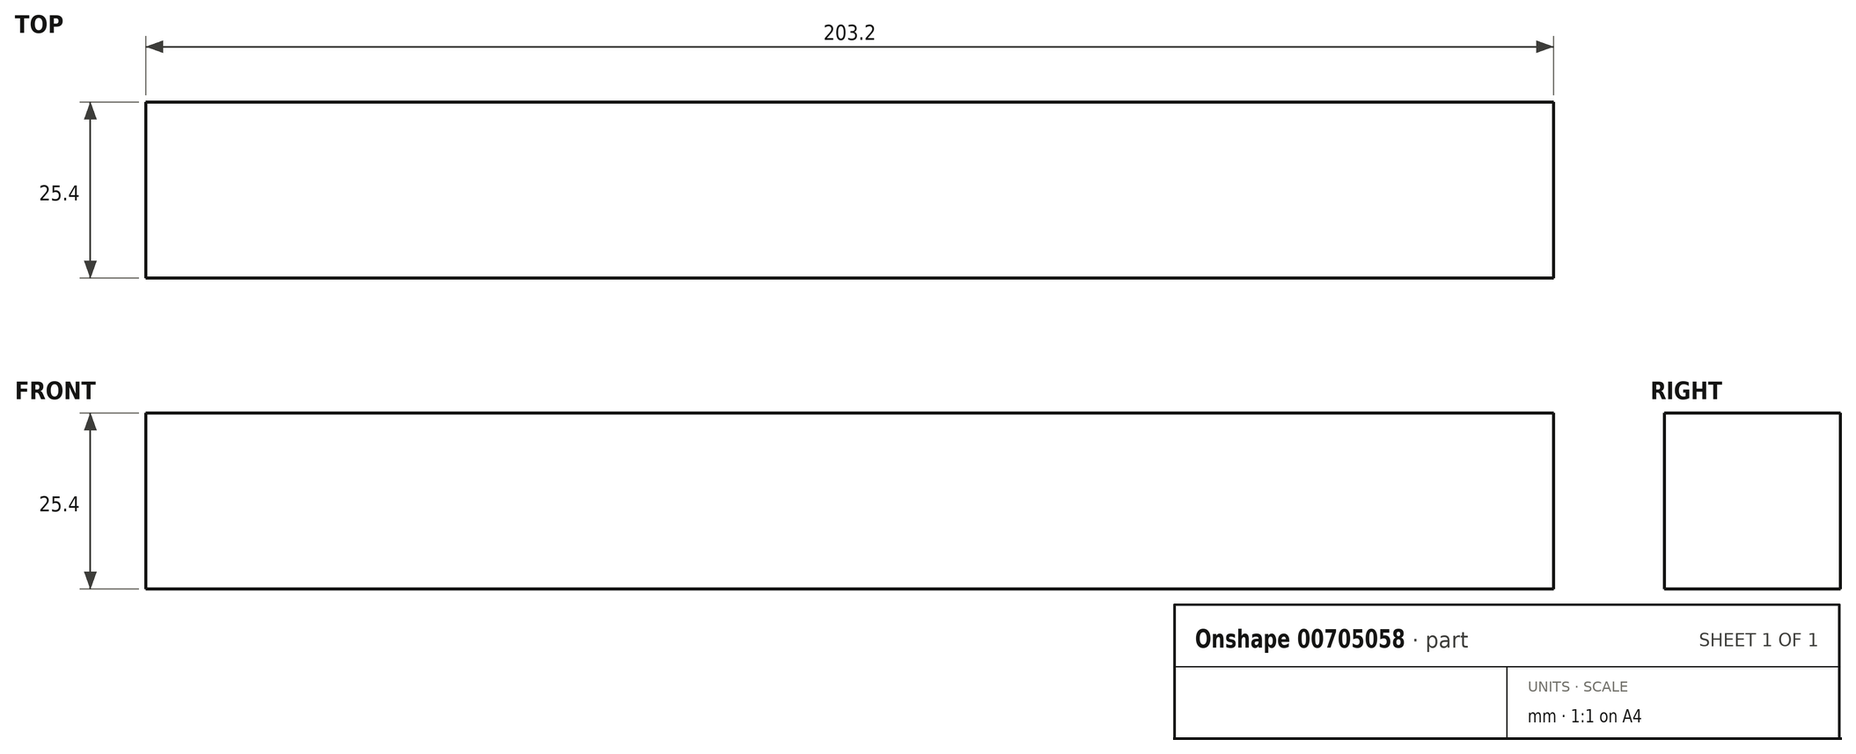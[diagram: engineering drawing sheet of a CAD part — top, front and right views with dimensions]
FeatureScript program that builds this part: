
annotation { "Feature Type Name" : "Feature", "Feature Type Description" : "" }
export const myFeature = defineFeature(function(context is Context, id is Id, definition is map)
    precondition{}
    {
        {
            var Q0;
            Q0=qCreatedBy(makeId("Top.planeOp"),FACE);
            var sketch = newSketch(context, id + "F0", { "sketchPlane" : qUnion([Q0])});
            skLineSegment(sketch, "E0.bottom", {"start": v(0, 0) * mm, "end": v(-203.2, 0) * mm});
            skLineSegment(sketch, "E0.top", {"start": v(0, 25.4) * mm, "end": v(-203.2, 25.4) * mm});
            skLineSegment(sketch, "E0.left", {"start": v(0, 0) * mm, "end": v(0, 25.4) * mm});
            skLineSegment(sketch, "E0.right", {"start": v(-203.2, 0) * mm, "end": v(-203.2, 25.4) * mm});
            skSolve(sketch);
        }
        {
            var Q0;
            Q0=makeQuery(id+"F0.imprint","IMPRINT",FACE,{"disambiguationData":[TD([[makeQuery(id+"F0.imprint","IMPRINT",EDGE,{"derivedFrom":sQuery(id+"F0.wireOp",EDGE,"E0.bottom")}),-1.0]])]});
            extrude(context, id + "F1", {"entities" : qUnion([Q0]), "depth" : 25.4 * mm, "offsetDistance" : 25.4 * mm});
        }
    });
